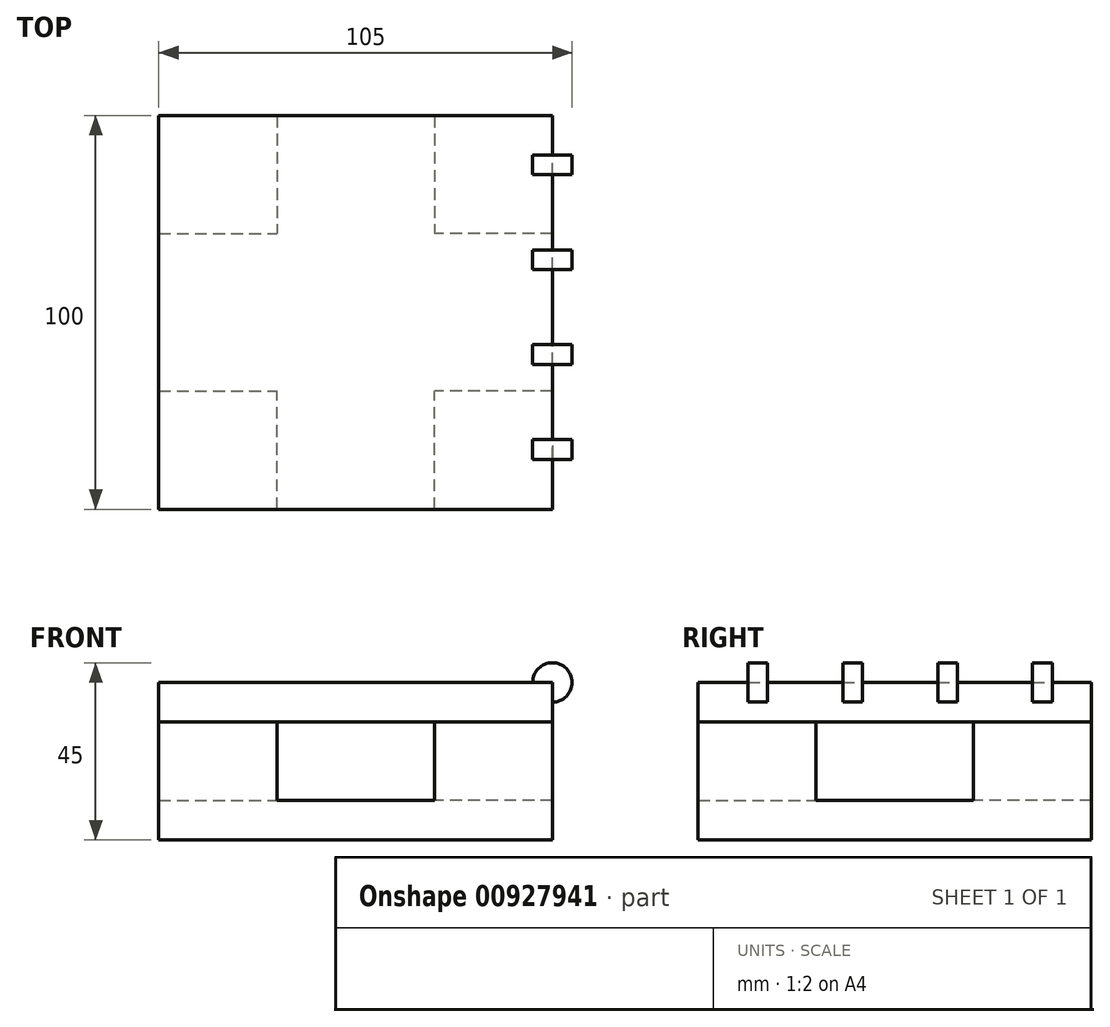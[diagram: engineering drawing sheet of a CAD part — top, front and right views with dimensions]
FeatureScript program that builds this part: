
annotation { "Feature Type Name" : "Feature", "Feature Type Description" : "" }
export const myFeature = defineFeature(function(context is Context, id is Id, definition is map)
    precondition{}
    {
        {
            var Q0;
            Q0=qCreatedBy(makeId("Top.planeOp"),FACE);
            var sketch = newSketch(context, id + "F0", { "sketchPlane" : qUnion([Q0])});
            skLineSegment(sketch, "E0.bottom", {"start": v(50, 50) * mm, "end": v(-50, 50) * mm});
            skLineSegment(sketch, "E0.top", {"start": v(50, -50) * mm, "end": v(-50, -50) * mm});
            skLineSegment(sketch, "E0.left", {"start": v(50, 50) * mm, "end": v(50, -50) * mm});
            skLineSegment(sketch, "E0.right", {"start": v(-50, 50) * mm, "end": v(-50, -50) * mm});
            skPoint(sketch, "E0.middle", {"position": v(0, 0) * mm});
            skSolve(sketch);
        }
        {
            var Q0;
            Q0 = qSketchRegion(id + "F0", true);
            extrude(context, id + "F1", {"entities" : qUnion([Q0]), "depth" : 10 * mm, "offsetDistance" : 25 * mm});
        }
        {
            var Q0;
            Q0=makeQuery(id+"F1.opExtrude","CAP_FACE",FACE,{"disambiguationData":[OSD([sQuery(id+"F0.wireOp",EDGE,"E0.bottom"),sQuery(id+"F0.wireOp",EDGE,"E0.top"),sQuery(id+"F0.wireOp",EDGE,"E0.left"),sQuery(id+"F0.wireOp",EDGE,"E0.right")])],"isStart":false});
            var sketch = newSketch(context, id + "F2", { "sketchPlane" : qUnion([Q0])});
            skLineSegment(sketch, "E1.bottom", {"start": v(-50, 50) * mm, "end": v(-20, 50) * mm});
            skLineSegment(sketch, "E1.top", {"start": v(-50, 20) * mm, "end": v(-20, 20) * mm});
            skLineSegment(sketch, "E1.left", {"start": v(-50, 50) * mm, "end": v(-50, 20) * mm});
            skLineSegment(sketch, "E1.right", {"start": v(-20, 50) * mm, "end": v(-20, 20) * mm});
            skLineSegment(sketch, "E2.MirrorCS", {"start": v(50, 50) * mm, "end": v(20, 50) * mm});
            skLineSegment(sketch, "E3.MirrorCS", {"start": v(20, 50) * mm, "end": v(20, 20) * mm});
            skLineSegment(sketch, "E4.MirrorCS", {"start": v(50, 20) * mm, "end": v(20, 20) * mm});
            skLineSegment(sketch, "E5.MirrorCS", {"start": v(50, 50) * mm, "end": v(50, 20) * mm});
            skLineSegment(sketch, "E6.MirrorCS", {"start": v(-50, -20) * mm, "end": v(-20, -20) * mm});
            skLineSegment(sketch, "E7.MirrorCS", {"start": v(-50, -50) * mm, "end": v(-50, -20) * mm});
            skLineSegment(sketch, "E8.MirrorCS", {"start": v(-50, -50) * mm, "end": v(-20, -50) * mm});
            skLineSegment(sketch, "E9.MirrorCS", {"start": v(-20, -50) * mm, "end": v(-20, -20) * mm});
            skLineSegment(sketch, "E10.MirrorCS", {"start": v(50, -20) * mm, "end": v(20, -20) * mm});
            skLineSegment(sketch, "E11.MirrorCS", {"start": v(20, -50) * mm, "end": v(20, -20) * mm});
            skLineSegment(sketch, "E12.MirrorCS", {"start": v(50, -50) * mm, "end": v(20, -50) * mm});
            skLineSegment(sketch, "E13.MirrorCS", {"start": v(50, -50) * mm, "end": v(50, -20) * mm});
            skSolve(sketch);
        }
        {
            var Q0;
            Q0 = qSketchRegion(id + "F2", true);
            extrude(context, id + "F3", {"entities" : qUnion([Q0]), "operationType" : NewBodyOperationType.ADD, "depth" : 20 * mm, "offsetDistance" : 25 * mm});
        }
        {
            var Q0;
            Q0=qCreatedBy(makeId("Top.planeOp"),FACE);
            cPlane(context, id + "F4", {"entities" : qUnion([Q0]), "cplaneType" : CPlaneType.OFFSET, "offset" : 30 * mm, "width" : 150 * mm, "height" : 150 * mm});
        }
        {
            var Q0;
            Q0=qCreatedBy(id+"F4.planeOp",FACE);
            var sketch = newSketch(context, id + "F5", { "sketchPlane" : qUnion([Q0])});
            skLineSegment(sketch, "E14.bottom", {"start": v(-50, 50) * mm, "end": v(50, 50) * mm});
            skLineSegment(sketch, "E14.top", {"start": v(-50, -50) * mm, "end": v(50, -50) * mm});
            skLineSegment(sketch, "E14.left", {"start": v(-50, 50) * mm, "end": v(-50, -50) * mm});
            skLineSegment(sketch, "E14.right", {"start": v(50, 50) * mm, "end": v(50, -50) * mm});
            skSolve(sketch);
        }
        {
            var Q0;
            Q0 = qSketchRegion(id + "F5", true);
            extrude(context, id + "F6", {"entities" : qUnion([Q0]), "depth" : 10 * mm, "offsetDistance" : 25 * mm});
        }
        {
            var Q0;
            Q0=makeQuery(id+"F6.opExtrude","CAP_FACE",FACE,{"disambiguationData":[OSD([sQuery(id+"F5.wireOp",EDGE,"E14.bottom"),sQuery(id+"F5.wireOp",EDGE,"E14.top"),sQuery(id+"F5.wireOp",EDGE,"E14.left"),sQuery(id+"F5.wireOp",EDGE,"E14.right")])],"isStart":false});
            var sketch = newSketch(context, id + "F7", { "sketchPlane" : qUnion([Q0])});
            skLineSegment(sketch, "E15", {"start": v(50, 40) * mm, "end": v(45, 40) * mm});
            skLineSegment(sketch, "E16", {"start": v(45, 40) * mm, "end": v(45, 35) * mm});
            skLineSegment(sketch, "E17", {"start": v(45, 35) * mm, "end": v(50, 35) * mm});
            skLineSegment(sketch, "E18.1.0.0", {"start": v(50, 15.9) * mm, "end": v(45, 15.9) * mm});
            skLineSegment(sketch, "E18.1.0.1", {"start": v(45, 15.9) * mm, "end": v(45, 10.9) * mm});
            skLineSegment(sketch, "E18.1.0.2", {"start": v(45, 10.9) * mm, "end": v(50, 10.9) * mm});
            skLineSegment(sketch, "E18.2.0.0", {"start": v(50, -8.2) * mm, "end": v(45, -8.2) * mm});
            skLineSegment(sketch, "E18.2.0.1", {"start": v(45, -8.2) * mm, "end": v(45, -13.2) * mm});
            skLineSegment(sketch, "E18.2.0.2", {"start": v(45, -13.2) * mm, "end": v(50, -13.2) * mm});
            skLineSegment(sketch, "E18.direction1", {"start": v(45, 40) * mm, "end": v(45, 15.9) * mm, "construction": true});
            skLineSegment(sketch, "E19.0.3.0", {"start": v(50, -32.3) * mm, "end": v(45, -32.3) * mm});
            skLineSegment(sketch, "E19.3.3.0", {"start": v(45, -32.3) * mm, "end": v(45, -37.3) * mm});
            skLineSegment(sketch, "E19.6.3.0", {"start": v(45, -37.3) * mm, "end": v(50, -37.3) * mm});
            skSolve(sketch);
        }
        {
            var Q0;
            {var subQ0=sQuery(id+"F7.wireOp",EDGE,"E15");Q0=makeQuery(id+"F7.imprint","IMPRINT",FACE,{"disambiguationData":[TD([[makeQuery(id+"F7.imprint","IMPRINT",EDGE,{"derivedFrom":subQ0}),1.0]])]});}
            var Q1;
            {var subQ0=sQuery(id+"F7.wireOp",EDGE,"E18.1.0.0");Q1=makeQuery(id+"F7.imprint","IMPRINT",FACE,{"disambiguationData":[TD([[makeQuery(id+"F7.imprint","IMPRINT",EDGE,{"derivedFrom":subQ0}),1.0]])]});}
            var Q2;
            {var subQ0=sQuery(id+"F7.wireOp",EDGE,"E18.2.0.0");Q2=makeQuery(id+"F7.imprint","IMPRINT",FACE,{"disambiguationData":[TD([[makeQuery(id+"F7.imprint","IMPRINT",EDGE,{"derivedFrom":subQ0}),1.0]])]});}
            var Q3;
            {var subQ0=sQuery(id+"F7.wireOp",EDGE,"E19.0.3.0");Q3=makeQuery(id+"F7.imprint","IMPRINT",FACE,{"disambiguationData":[TD([[makeQuery(id+"F7.imprint","IMPRINT",EDGE,{"derivedFrom":subQ0}),1.0]])]});}
            var Q4;
            Q4=makeQuery(id+"F6.opExtrude","CAP_EDGE",EDGE,{"disambiguationData":[OSD([sQuery(id+"F5.wireOp",EDGE,"E14.right")])],"isStart":false});
            revolve(context, id + "F8", {"operationType" : NewBodyOperationType.ADD, "surfaceOperationType" : NewSurfaceOperationType.NEW, "entities" : qUnion([Q0, Q1, Q2, Q3]), "axis" : qUnion([Q4]), "revolveType" : RevolveType.FULL});
        }
    });
